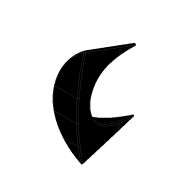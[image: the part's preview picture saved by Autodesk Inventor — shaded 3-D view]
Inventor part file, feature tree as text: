
AUTODESK INVENTOR PART (.ipt)
format: ipt  version: 2020 (Build 240168000, 168)  size: 667,136 bytes
history: native  units: in
note: dims shown in document units (in); Inventor stores cm internally (conversion verified against a paired STEP export)
features: extrude x3, fillet x3, sketch x3, projected_geometry x2, plane x1
ambient origin geometry x8: Origin, YZ Plane, XZ Plane, XY Plane, X Axis, Y Axis, Z Axis, Center Point
bodies: Solid1 (feature_tree)
feature tree (12):
  extrude  "Extrusion1"  Depth=4.6457in
  fillet  "Fillet1"  Radius=0.0787in
  fillet  "Fillet2"  Radius=0.0787in
  fillet  "Fillet3"  Radius=0.3543in
  plane  "Work Plane1"
  extrude  "Extrusion2"  Depth=0.2339in
  extrude  "Extrusion3"  Depth=0.2362in
  sketch  "Sketch1"  dims[d0=1.9685in d1=0.0in d2=4.6457in d3=0.0787in d4=0.0787in d5=0.3543in]
  sketch  "Sketch2"  dims[d6=1.1897in d7=0.2339in]
  sketch  "Sketch3"  dims[d8=1.6535in d9=0.0in d10=0.2362in d11=0.2362in d12=1.6535in d13=0.0in]
  projected_geometry  "Projected Loop1"
  projected_geometry  "Projected Loop2"
